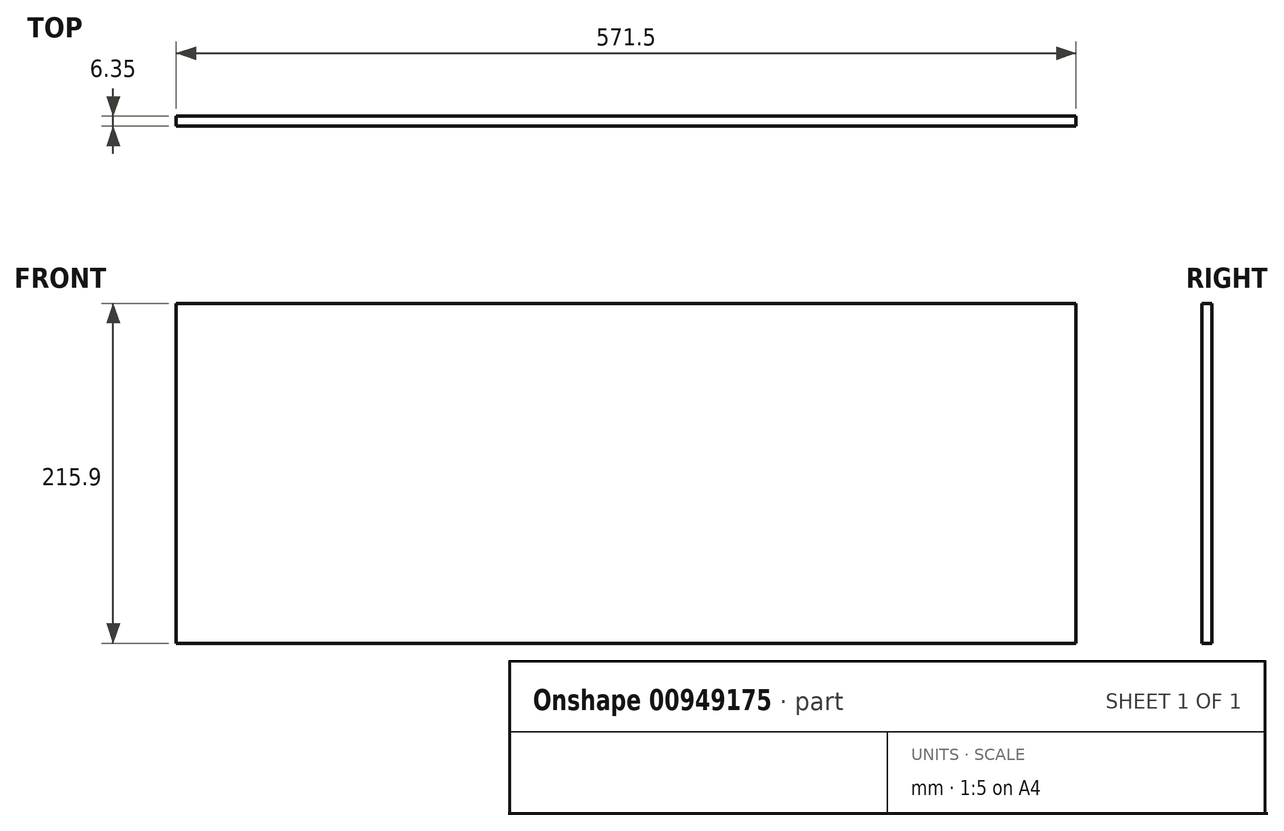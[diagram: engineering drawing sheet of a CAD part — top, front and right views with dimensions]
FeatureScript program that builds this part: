
annotation { "Feature Type Name" : "Feature", "Feature Type Description" : "" }
export const myFeature = defineFeature(function(context is Context, id is Id, definition is map)
    precondition{}
    {
        {
            var Q0;
            Q0=qCreatedBy(makeId("Front.planeOp"),FACE);
            var sketch = newSketch(context, id + "F0", { "sketchPlane" : qUnion([Q0])});
            skLineSegment(sketch, "E0.bottom", {"start": v(-290.57, 102.13) * mm, "end": v(280.93, 102.13) * mm});
            skLineSegment(sketch, "E0.top", {"start": v(-290.57, -113.77) * mm, "end": v(280.93, -113.77) * mm});
            skLineSegment(sketch, "E0.left", {"start": v(-290.57, 102.13) * mm, "end": v(-290.57, -113.77) * mm});
            skLineSegment(sketch, "E0.right", {"start": v(280.93, 102.13) * mm, "end": v(280.93, -113.77) * mm});
            skSolve(sketch);
        }
        {
            var Q0;
            Q0=makeQuery(id+"F0.imprint","IMPRINT",FACE,{"disambiguationData":[TD([[makeQuery(id+"F0.imprint","IMPRINT",EDGE,{"derivedFrom":sQuery(id+"F0.wireOp",EDGE,"E0.bottom")}),-1.0]])]});
            extrude(context, id + "F1", {"entities" : qUnion([Q0]), "depth" : 6.35 * mm, "offsetDistance" : 25.4 * mm});
        }
    });
